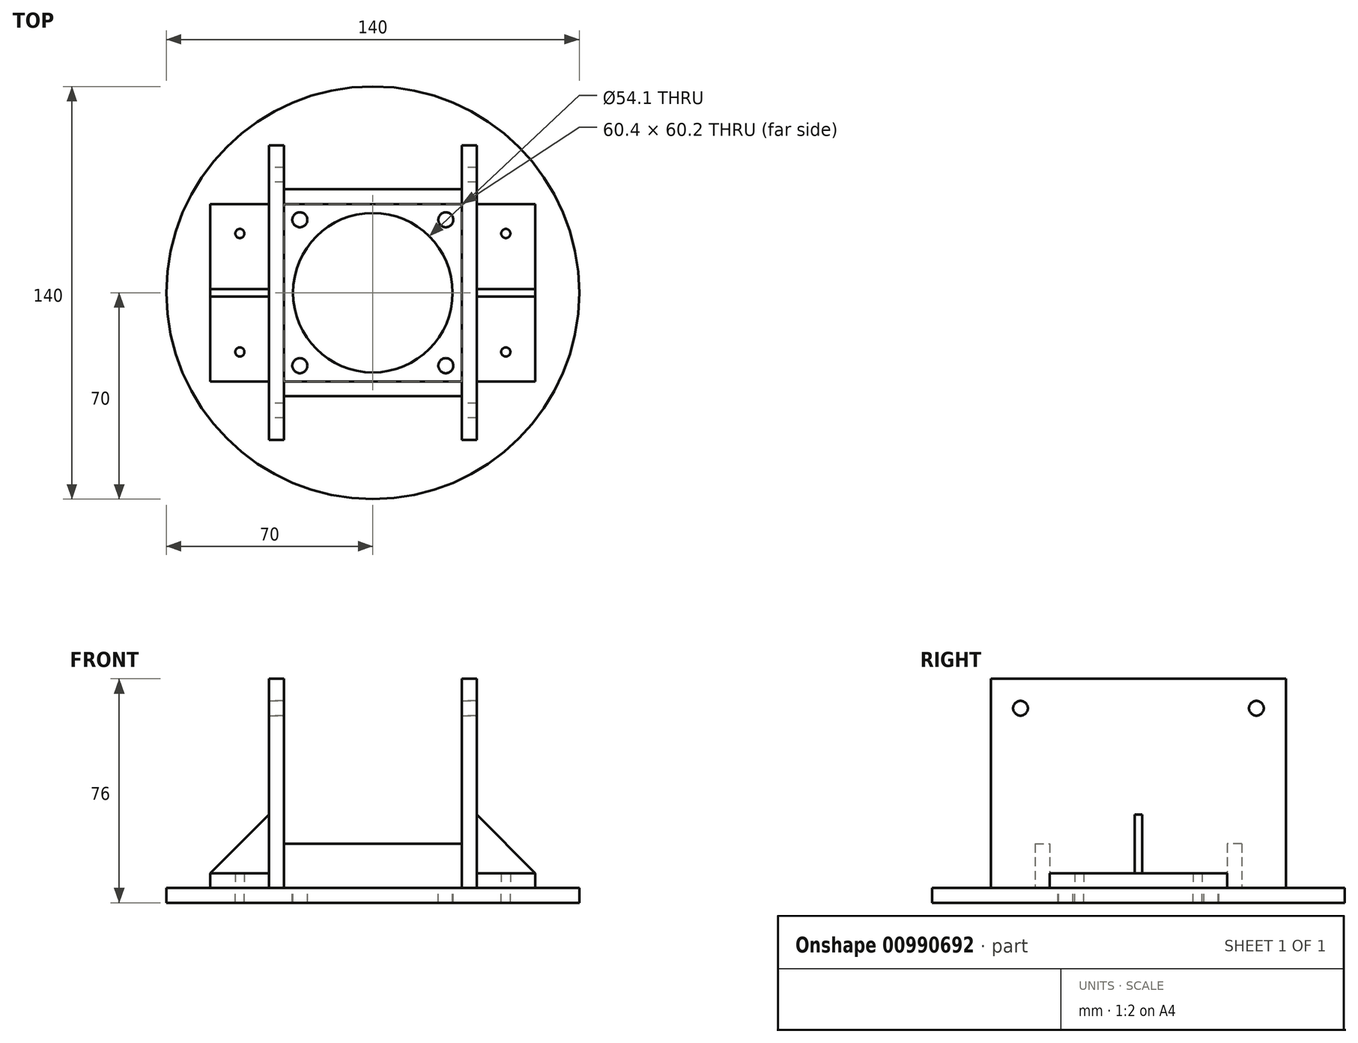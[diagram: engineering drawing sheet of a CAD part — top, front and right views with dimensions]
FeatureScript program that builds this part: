
annotation { "Feature Type Name" : "Feature", "Feature Type Description" : "" }
export const myFeature = defineFeature(function(context is Context, id is Id, definition is map)
    precondition{}
    {
        {
            assignVariable(context, id + "F0", {"name" : "Thickness", "anyValue" : 5});
        }
        {
            var Q0;
            Q0=qCreatedBy(makeId("Top.planeOp"),FACE);
            var sketch = newSketch(context, id + "F1", { "sketchPlane" : qUnion([Q0])});
            skLineSegment(sketch, "E0.bottom", {"start": v(-35.1, 30.1) * mm, "end": v(-55.1, 30.1) * mm});
            skLineSegment(sketch, "E0.top", {"start": v(-35.1, -30.1) * mm, "end": v(-55.1, -30.1) * mm});
            skLineSegment(sketch, "E0.left", {"start": v(-35.1, 30.1) * mm, "end": v(-35.1, -30.1) * mm});
            skLineSegment(sketch, "E0.right", {"start": v(-55.1, 30.1) * mm, "end": v(-55.1, -30.1) * mm});
            skPoint(sketch, "E0.middle", {"position": v(-45.1, 0) * mm});
            skCircle(sketch, "E1", {"center": v(-45.1, 20.1) * mm, "radius": 1.55 * mm});
            skCircle(sketch, "E2", {"center": v(-45.1, -20.1) * mm, "radius": 1.55 * mm});
            skSolve(sketch);
        }
        {
            var Q0;
            Q0 = qSketchRegion(id + "F1", true);
            extrude(context, id + "F2", {"entities" : qUnion([Q0]), "depth" : (getVariable(context, 'Thickness')) * mm, "offsetDistance" : 25 * mm});
        }
        {
            var Q0;
            Q0=qCreatedBy(makeId("Top.planeOp"),FACE);
            var sketch = newSketch(context, id + "F3", { "sketchPlane" : qUnion([Q0])});
            skCircle(sketch, "E3", {"center": v(0, 0) * mm, "radius": 70.71 * mm});
            skLineSegment(sketch, "E4.bottom", {"start": v(50, 50) * mm, "end": v(-50, 50) * mm, "construction": true});
            skLineSegment(sketch, "E4.top", {"start": v(50, -50) * mm, "end": v(-50, -50) * mm, "construction": true});
            skLineSegment(sketch, "E4.left", {"start": v(50, 50) * mm, "end": v(50, -50) * mm, "construction": true});
            skLineSegment(sketch, "E4.right", {"start": v(-50, 50) * mm, "end": v(-50, -50) * mm, "construction": true});
            skSolve(sketch);
        }
        {
            var Q0;
            Q0=qCreatedBy(makeId("Top.planeOp"),FACE);
            var sketch = newSketch(context, id + "F4", { "sketchPlane" : qUnion([Q0])});
            skLineSegment(sketch, "E5.bottom", {"start": v(35.2, -50) * mm, "end": v(30.2, -50) * mm});
            skLineSegment(sketch, "E5.top", {"start": v(35.2, 50) * mm, "end": v(30.2, 50) * mm});
            skLineSegment(sketch, "E5.left", {"start": v(35.2, -50) * mm, "end": v(35.2, 50) * mm});
            skLineSegment(sketch, "E5.right", {"start": v(30.2, -50) * mm, "end": v(30.2, 50) * mm});
            skPoint(sketch, "E5.middle", {"position": v(32.7, 0) * mm});
            skLineSegment(sketch, "E6.MirrorCS", {"start": v(-35.2, 50) * mm, "end": v(-30.2, 50) * mm});
            skLineSegment(sketch, "E7.MirrorCS", {"start": v(-35.2, -50) * mm, "end": v(-30.2, -50) * mm});
            skLineSegment(sketch, "E8.MirrorCS", {"start": v(-35.2, -50) * mm, "end": v(-35.2, 50) * mm});
            skLineSegment(sketch, "E9.MirrorCS", {"start": v(-30.2, -50) * mm, "end": v(-30.2, 50) * mm});
            skPoint(sketch, "E10.MirrorP", {"position": v(-32.7, 0) * mm});
            skSolve(sketch);
        }
        {
            var Q0;
            Q0 = qSketchRegion(id + "F4", true);
            extrude(context, id + "F5", {"entities" : qUnion([Q0]), "depth" : 71 * mm, "offsetDistance" : 25 * mm});
        }
        {
            var Q0;
            Q0=makeQuery(id+"F5.opExtrude","SWEPT_FACE",FACE,{"disambiguationData":[OSD([sQuery(id+"F4.wireOp",EDGE,"E5.left")])]});
            var sketch = newSketch(context, id + "F6", { "sketchPlane" : qUnion([Q0])});
            skCircle(sketch, "E11", {"center": v(-40, 61) * mm, "radius": 2.5 * mm});
            skCircle(sketch, "E12.MirrorC", {"center": v(40, 61) * mm, "radius": 2.5 * mm});
            skSolve(sketch);
        }
        {
            var Q0;
            Q0 = qSketchRegion(id + "F6", true);
            extrude(context, id + "F7", {"entities" : qUnion([Q0]), "operationType" : NewBodyOperationType.REMOVE, "endBound" : BoundingType.THROUGH_ALL, "oppositeDirection" : true, "depth" : 25 * mm, "offsetDistance" : 25 * mm});
        }
        {
            var Q0;
            Q0=qCreatedBy(makeId("Top.planeOp"),FACE);
            var sketch = newSketch(context, id + "F8", { "sketchPlane" : qUnion([Q0])});
            skLineSegment(sketch, "E13.bottom", {"start": v(-30.2, 35.1) * mm, "end": v(30.2, 35.1) * mm});
            skLineSegment(sketch, "E13.top", {"start": v(-30.2, 30.1) * mm, "end": v(30.2, 30.1) * mm});
            skLineSegment(sketch, "E13.left", {"start": v(-30.2, 35.1) * mm, "end": v(-30.2, 30.1) * mm});
            skLineSegment(sketch, "E13.right", {"start": v(30.2, 35.1) * mm, "end": v(30.2, 30.1) * mm});
            skLineSegment(sketch, "E14.MirrorCS", {"start": v(-30.2, -35.1) * mm, "end": v(-30.2, -30.1) * mm});
            skLineSegment(sketch, "E15.MirrorCS", {"start": v(30.2, -35.1) * mm, "end": v(30.2, -30.1) * mm});
            skLineSegment(sketch, "E16.MirrorCS", {"start": v(-30.2, -30.1) * mm, "end": v(30.2, -30.1) * mm});
            skLineSegment(sketch, "E17.MirrorCS", {"start": v(-30.2, -35.1) * mm, "end": v(30.2, -35.1) * mm});
            skSolve(sketch);
        }
        {
            var Q0;
            Q0 = qSketchRegion(id + "F8", true);
            extrude(context, id + "F9", {"entities" : qUnion([Q0]), "operationType" : NewBodyOperationType.ADD, "depth" : 15 * mm, "offsetDistance" : 25 * mm});
        }
        {
            var Q0;
            Q0=qCreatedBy(makeId("Front.planeOp"),FACE);
            var sketch = newSketch(context, id + "F10", { "sketchPlane" : qUnion([Q0])});
            skLineSegment(sketch, "E18", {"start": v(-55.1, 5) * mm, "end": v(-35.2, 5) * mm});
            skLineSegment(sketch, "E19", {"start": v(-35.2, 5) * mm, "end": v(-35.2, 24.9) * mm});
            skLineSegment(sketch, "E20", {"start": v(-35.2, 24.9) * mm, "end": v(-55.1, 5) * mm});
            skSolve(sketch);
        }
        {
            var Q0;
            Q0=makeQuery(id+"F10.imprint","IMPRINT",FACE,{"disambiguationData":[TD([[makeQuery(id+"F10.imprint","IMPRINT",EDGE,{"derivedFrom":sQuery(id+"F10.wireOp",EDGE,"E18")}),1.0]])]});
            extrude(context, id + "F11", {"entities" : qUnion([Q0]), "operationType" : NewBodyOperationType.ADD, "endBound" : BoundingType.SYMMETRIC, "depth" : (getVariable(context, 'Thickness') / 2) * mm, "offsetDistance" : 25 * mm});
        }
        {
            var Q0;
            Q0=makeQuery(id+"F2.opExtrude","SWEPT_BODY",BODY,{"disambiguationData":[OSD([sQuery(id+"F1.wireOp",EDGE,"E0.bottom"),sQuery(id+"F1.wireOp",EDGE,"E0.top"),sQuery(id+"F1.wireOp",EDGE,"E0.left"),sQuery(id+"F1.wireOp",EDGE,"E0.right"),sQuery(id+"F1.wireOp",EDGE,"E1"),sQuery(id+"F1.wireOp",EDGE,"E2")])]});
            var Q1;
            Q1=qCreatedBy(makeId("Right.planeOp"),FACE);
            mirror(context, id + "F12", {"entities" : qUnion([Q0]), "mirrorPlane" : qUnion([Q1])});
        }
        {
            var Q0;
            Q0=qCreatedBy(makeId("Top.planeOp"),FACE);
            var sketch = newSketch(context, id + "F13", { "sketchPlane" : qUnion([Q0])});
            skCircle(sketch, "E21", {"center": v(0, 0) * mm, "radius": 27.05 * mm});
            skLineSegment(sketch, "E22.bottom", {"start": v(30, -30) * mm, "end": v(-30, -30) * mm, "construction": true});
            skLineSegment(sketch, "E22.top", {"start": v(30, 30) * mm, "end": v(-30, 30) * mm, "construction": true});
            skLineSegment(sketch, "E22.left", {"start": v(30, -30) * mm, "end": v(30, 30) * mm, "construction": true});
            skLineSegment(sketch, "E22.right", {"start": v(-30, -30) * mm, "end": v(-30, 30) * mm, "construction": true});
            skLineSegment(sketch, "E23.bottom", {"start": v(24.75, -24.75) * mm, "end": v(-24.75, -24.75) * mm, "construction": true});
            skLineSegment(sketch, "E23.top", {"start": v(24.75, 24.75) * mm, "end": v(-24.75, 24.75) * mm, "construction": true});
            skLineSegment(sketch, "E23.left", {"start": v(24.75, -24.75) * mm, "end": v(24.75, 24.75) * mm, "construction": true});
            skLineSegment(sketch, "E23.right", {"start": v(-24.75, -24.75) * mm, "end": v(-24.75, 24.75) * mm, "construction": true});
            skCircle(sketch, "E24", {"center": v(-24.75, -24.75) * mm, "radius": 2.55 * mm});
            skCircle(sketch, "E25.1.0", {"center": v(24.75, -24.75) * mm, "radius": 2.55 * mm});
            skCircle(sketch, "E25.2.0", {"center": v(24.75, 24.75) * mm, "radius": 2.55 * mm});
            skCircle(sketch, "E25.3.0", {"center": v(-24.75, 24.75) * mm, "radius": 2.55 * mm});
            skCircle(sketch, "E26", {"center": v(0, 0) * mm, "radius": 70 * mm});
            skCircle(sketch, "E27", {"center": v(45.1, -20.1) * mm, "radius": 1.55 * mm});
            skCircle(sketch, "E28.MirrorC", {"center": v(45.1, 20.1) * mm, "radius": 1.55 * mm});
            skCircle(sketch, "E29.MirrorC", {"center": v(-45.1, -20.1) * mm, "radius": 1.55 * mm});
            skCircle(sketch, "E30.MirrorC", {"center": v(-45.1, 20.1) * mm, "radius": 1.55 * mm});
            skLineSegment(sketch, "E31", {"start": v(0, 0) * mm, "end": v(-28.28, 28.28) * mm, "construction": true});
            skCircle(sketch, "E32", {"center": v(-28.28, 28.28) * mm, "radius": 2.5 * mm, "construction": true});
            skCircle(sketch, "E33", {"center": v(0, 0) * mm, "radius": 40 * mm, "construction": true});
            skSolve(sketch);
        }
        {
            var Q0;
            Q0 = qSketchRegion(id + "F13", true);
            extrude(context, id + "F14", {"entities" : qUnion([Q0]), "oppositeDirection" : true, "depth" : 5 * mm, "offsetDistance" : 25 * mm});
        }
    });
